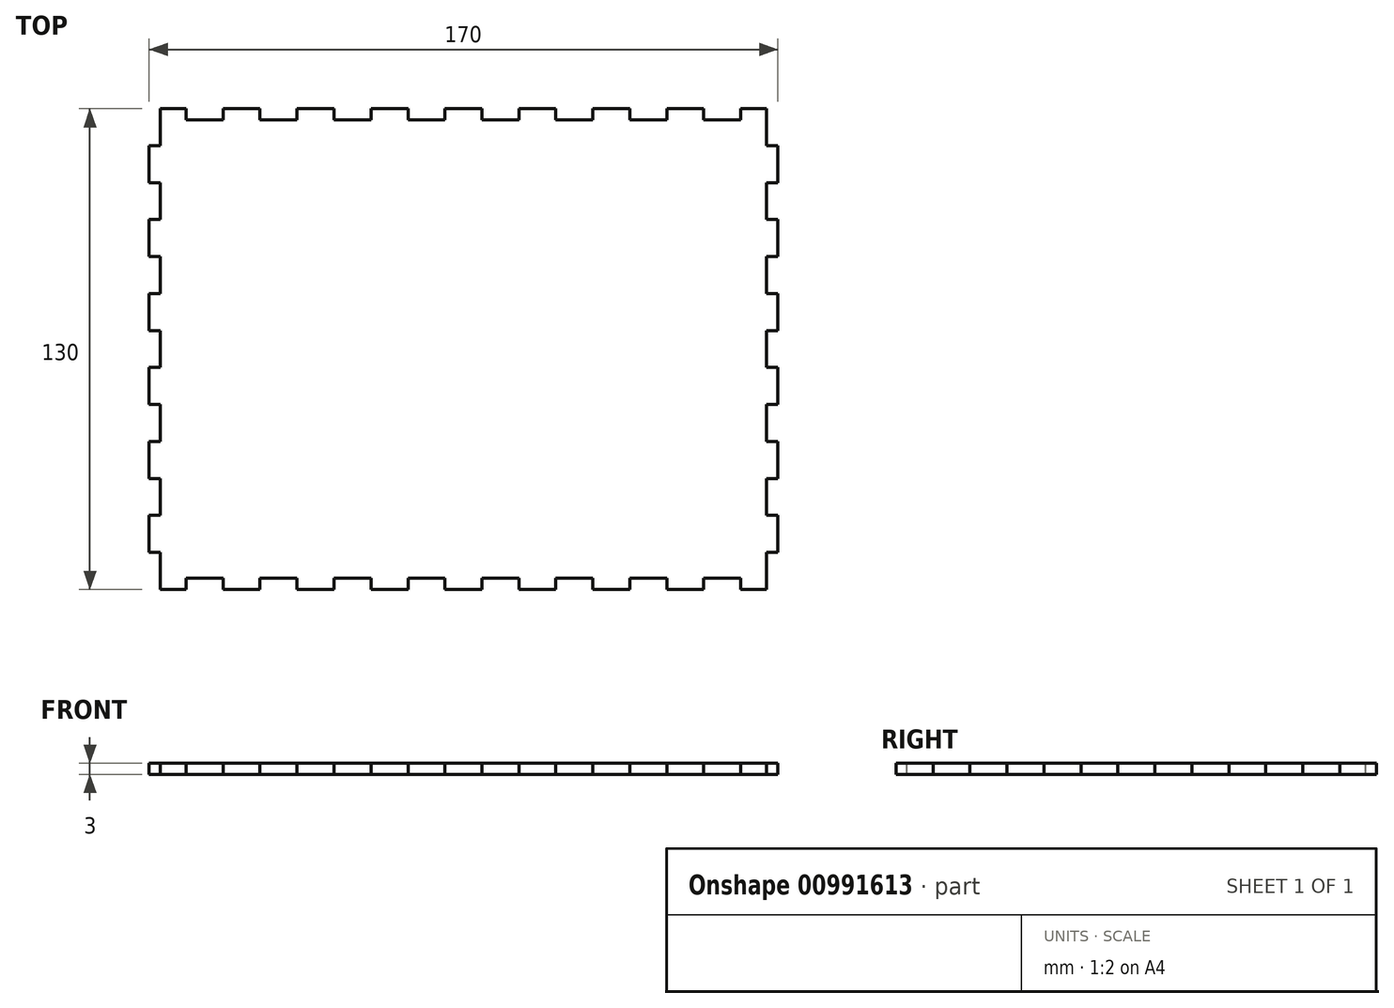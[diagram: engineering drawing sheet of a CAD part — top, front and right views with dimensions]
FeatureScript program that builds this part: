
annotation { "Feature Type Name" : "Feature", "Feature Type Description" : "" }
export const myFeature = defineFeature(function(context is Context, id is Id, definition is map)
    precondition{}
    {
        {
            var Q0;
            Q0=qCreatedBy(makeId("Top.planeOp"),FACE);
            var sketch = newSketch(context, id + "F0", { "sketchPlane" : qUnion([Q0])});
            skLineSegment(sketch, "E0.bottom", {"start": v(85, -65) * mm, "end": v(-85, -65) * mm});
            skLineSegment(sketch, "E0.top", {"start": v(85, 65) * mm, "end": v(-85, 65) * mm});
            skLineSegment(sketch, "E0.left", {"start": v(85, -65) * mm, "end": v(85, 65) * mm});
            skLineSegment(sketch, "E0.right", {"start": v(-85, -65) * mm, "end": v(-85, 65) * mm});
            skPoint(sketch, "E0.middle", {"position": v(0, 0) * mm});
            skSolve(sketch);
        }
        {
            var Q0;
            Q0=qSketchRegion(id+"F0",true);
            extrude(context, id + "F1", {"entities" : qUnion([Q0]), "depth" : 3 * mm, "offsetDistance" : 25 * mm});
        }
        {
            var Q0;
            Q0=makeQuery(id+"F1.opExtrude","CAP_FACE",FACE,{"disambiguationData":[OSD([sQuery(id+"F0.wireOp",EDGE,"E0.bottom"),sQuery(id+"F0.wireOp",EDGE,"E0.top"),sQuery(id+"F0.wireOp",EDGE,"E0.left"),sQuery(id+"F0.wireOp",EDGE,"E0.right")])],"isStart":false});
            var sketch = newSketch(context, id + "F2", { "sketchPlane" : qUnion([Q0])});
            skLineSegment(sketch, "E1.bottom", {"start": v(-75, -65) * mm, "end": v(-65, -65) * mm});
            skLineSegment(sketch, "E1.top", {"start": v(-75, -62) * mm, "end": v(-65, -62) * mm});
            skLineSegment(sketch, "E1.left", {"start": v(-75, -65) * mm, "end": v(-75, -62) * mm});
            skLineSegment(sketch, "E1.right", {"start": v(-65, -65) * mm, "end": v(-65, -62) * mm});
            skLineSegment(sketch, "E2.1.0.0", {"start": v(-55, -65) * mm, "end": v(-45, -65) * mm});
            skLineSegment(sketch, "E2.1.0.1", {"start": v(-55, -62) * mm, "end": v(-45, -62) * mm});
            skLineSegment(sketch, "E2.1.0.2", {"start": v(-55, -65) * mm, "end": v(-55, -62) * mm});
            skLineSegment(sketch, "E2.1.0.3", {"start": v(-45, -65) * mm, "end": v(-45, -62) * mm});
            skLineSegment(sketch, "E2.2.0.0", {"start": v(-35, -65) * mm, "end": v(-25, -65) * mm});
            skLineSegment(sketch, "E2.2.0.1", {"start": v(-35, -62) * mm, "end": v(-25, -62) * mm});
            skLineSegment(sketch, "E2.2.0.2", {"start": v(-35, -65) * mm, "end": v(-35, -62) * mm});
            skLineSegment(sketch, "E2.2.0.3", {"start": v(-25, -65) * mm, "end": v(-25, -62) * mm});
            skLineSegment(sketch, "E2.3.0.0", {"start": v(-15, -65) * mm, "end": v(-5, -65) * mm});
            skLineSegment(sketch, "E2.3.0.1", {"start": v(-15, -62) * mm, "end": v(-5, -62) * mm});
            skLineSegment(sketch, "E2.3.0.2", {"start": v(-15, -65) * mm, "end": v(-15, -62) * mm});
            skLineSegment(sketch, "E2.3.0.3", {"start": v(-5, -65) * mm, "end": v(-5, -62) * mm});
            skLineSegment(sketch, "E2.4.0.0", {"start": v(5, -65) * mm, "end": v(15, -65) * mm});
            skLineSegment(sketch, "E2.4.0.1", {"start": v(5, -62) * mm, "end": v(15, -62) * mm});
            skLineSegment(sketch, "E2.4.0.2", {"start": v(5, -65) * mm, "end": v(5, -62) * mm});
            skLineSegment(sketch, "E2.4.0.3", {"start": v(15, -65) * mm, "end": v(15, -62) * mm});
            skLineSegment(sketch, "E2.5.0.0", {"start": v(25, -65) * mm, "end": v(35, -65) * mm});
            skLineSegment(sketch, "E2.5.0.1", {"start": v(25, -62) * mm, "end": v(35, -62) * mm});
            skLineSegment(sketch, "E2.5.0.2", {"start": v(25, -65) * mm, "end": v(25, -62) * mm});
            skLineSegment(sketch, "E2.5.0.3", {"start": v(35, -65) * mm, "end": v(35, -62) * mm});
            skLineSegment(sketch, "E2.6.0.0", {"start": v(45, -65) * mm, "end": v(55, -65) * mm});
            skLineSegment(sketch, "E2.6.0.1", {"start": v(45, -62) * mm, "end": v(55, -62) * mm});
            skLineSegment(sketch, "E2.6.0.2", {"start": v(45, -65) * mm, "end": v(45, -62) * mm});
            skLineSegment(sketch, "E2.6.0.3", {"start": v(55, -65) * mm, "end": v(55, -62) * mm});
            skLineSegment(sketch, "E2.7.0.0", {"start": v(65, -65) * mm, "end": v(75, -65) * mm});
            skLineSegment(sketch, "E2.7.0.1", {"start": v(65, -62) * mm, "end": v(75, -62) * mm});
            skLineSegment(sketch, "E2.7.0.2", {"start": v(65, -65) * mm, "end": v(65, -62) * mm});
            skLineSegment(sketch, "E2.7.0.3", {"start": v(75, -65) * mm, "end": v(75, -62) * mm});
            skLineSegment(sketch, "E2.direction1", {"start": v(-75, -65) * mm, "end": v(-55, -65) * mm, "construction": true});
            skLineSegment(sketch, "E3.bottom", {"start": v(-85, -65) * mm, "end": v(-82, -65) * mm});
            skLineSegment(sketch, "E3.top", {"start": v(-85, -55) * mm, "end": v(-82, -55) * mm});
            skLineSegment(sketch, "E3.left", {"start": v(-85, -65) * mm, "end": v(-85, -55) * mm});
            skLineSegment(sketch, "E3.right", {"start": v(-82, -65) * mm, "end": v(-82, -55) * mm});
            skLineSegment(sketch, "E4.0.1.0", {"start": v(-85, -45) * mm, "end": v(-82, -45) * mm});
            skLineSegment(sketch, "E4.0.1.1", {"start": v(-85, -35) * mm, "end": v(-82, -35) * mm});
            skLineSegment(sketch, "E4.0.1.2", {"start": v(-85, -45) * mm, "end": v(-85, -35) * mm});
            skLineSegment(sketch, "E4.0.1.3", {"start": v(-82, -45) * mm, "end": v(-82, -35) * mm});
            skLineSegment(sketch, "E4.0.2.0", {"start": v(-85, -25) * mm, "end": v(-82, -25) * mm});
            skLineSegment(sketch, "E4.0.2.1", {"start": v(-85, -15) * mm, "end": v(-82, -15) * mm});
            skLineSegment(sketch, "E4.0.2.2", {"start": v(-85, -25) * mm, "end": v(-85, -15) * mm});
            skLineSegment(sketch, "E4.0.2.3", {"start": v(-82, -25) * mm, "end": v(-82, -15) * mm});
            skLineSegment(sketch, "E4.0.3.0", {"start": v(-85, -5) * mm, "end": v(-82, -5) * mm});
            skLineSegment(sketch, "E4.0.3.1", {"start": v(-85, 5) * mm, "end": v(-82, 5) * mm});
            skLineSegment(sketch, "E4.0.3.2", {"start": v(-85, -5) * mm, "end": v(-85, 5) * mm});
            skLineSegment(sketch, "E4.0.3.3", {"start": v(-82, -5) * mm, "end": v(-82, 5) * mm});
            skLineSegment(sketch, "E4.0.4.0", {"start": v(-85, 15) * mm, "end": v(-82, 15) * mm});
            skLineSegment(sketch, "E4.0.4.1", {"start": v(-85, 25) * mm, "end": v(-82, 25) * mm});
            skLineSegment(sketch, "E4.0.4.2", {"start": v(-85, 15) * mm, "end": v(-85, 25) * mm});
            skLineSegment(sketch, "E4.0.4.3", {"start": v(-82, 15) * mm, "end": v(-82, 25) * mm});
            skLineSegment(sketch, "E4.0.5.0", {"start": v(-85, 35) * mm, "end": v(-82, 35) * mm});
            skLineSegment(sketch, "E4.0.5.1", {"start": v(-85, 45) * mm, "end": v(-82, 45) * mm});
            skLineSegment(sketch, "E4.0.5.2", {"start": v(-85, 35) * mm, "end": v(-85, 45) * mm});
            skLineSegment(sketch, "E4.0.5.3", {"start": v(-82, 35) * mm, "end": v(-82, 45) * mm});
            skLineSegment(sketch, "E4.0.6.0", {"start": v(-85, 55) * mm, "end": v(-82, 55) * mm});
            skLineSegment(sketch, "E4.0.6.1", {"start": v(-85, 65) * mm, "end": v(-82, 65) * mm});
            skLineSegment(sketch, "E4.0.6.2", {"start": v(-85, 55) * mm, "end": v(-85, 65) * mm});
            skLineSegment(sketch, "E4.0.6.3", {"start": v(-82, 55) * mm, "end": v(-82, 65) * mm});
            skLineSegment(sketch, "E4.direction1", {"start": v(-85, -65) * mm, "end": v(-60, -65) * mm, "construction": true});
            skLineSegment(sketch, "E4.direction2", {"start": v(-85, -65) * mm, "end": v(-85, -45) * mm, "construction": true});
            skLineSegment(sketch, "E5", {"start": v(85, 0) * mm, "end": v(-85, 0) * mm, "construction": true});
            skLineSegment(sketch, "E6", {"start": v(0, 65) * mm, "end": v(0, -65) * mm, "construction": true});
            skLineSegment(sketch, "E7.MirrorCS", {"start": v(85, -65) * mm, "end": v(85, -55) * mm});
            skLineSegment(sketch, "E8.MirrorCS", {"start": v(82, -45) * mm, "end": v(82, -35) * mm});
            skLineSegment(sketch, "E9.MirrorCS", {"start": v(85, -45) * mm, "end": v(85, -35) * mm});
            skLineSegment(sketch, "E10.MirrorCS", {"start": v(82, 15) * mm, "end": v(82, 25) * mm});
            skLineSegment(sketch, "E11.MirrorCS", {"start": v(85, 15) * mm, "end": v(85, 25) * mm});
            skLineSegment(sketch, "E12.MirrorCS", {"start": v(85, 55) * mm, "end": v(82, 55) * mm});
            skLineSegment(sketch, "E13.MirrorCS", {"start": v(85, -5) * mm, "end": v(85, 5) * mm});
            skLineSegment(sketch, "E14.MirrorCS", {"start": v(85, 55) * mm, "end": v(85, 65) * mm});
            skLineSegment(sketch, "E15.MirrorCS", {"start": v(85, -5) * mm, "end": v(82, -5) * mm});
            skLineSegment(sketch, "E16.MirrorCS", {"start": v(85, 65) * mm, "end": v(82, 65) * mm});
            skLineSegment(sketch, "E17.MirrorCS", {"start": v(82, 55) * mm, "end": v(82, 65) * mm});
            skLineSegment(sketch, "E18.MirrorCS", {"start": v(85, 15) * mm, "end": v(82, 15) * mm});
            skLineSegment(sketch, "E19.MirrorCS", {"start": v(85, -25) * mm, "end": v(85, -15) * mm});
            skLineSegment(sketch, "E20.MirrorCS", {"start": v(82, -5) * mm, "end": v(82, 5) * mm});
            skLineSegment(sketch, "E21.MirrorCS", {"start": v(85, -35) * mm, "end": v(82, -35) * mm});
            skLineSegment(sketch, "E22.MirrorCS", {"start": v(85, -55) * mm, "end": v(82, -55) * mm});
            skLineSegment(sketch, "E23.MirrorCS", {"start": v(85, -45) * mm, "end": v(82, -45) * mm});
            skLineSegment(sketch, "E24.MirrorCS", {"start": v(85, 25) * mm, "end": v(82, 25) * mm});
            skLineSegment(sketch, "E25.MirrorCS", {"start": v(85, 35) * mm, "end": v(82, 35) * mm});
            skLineSegment(sketch, "E26.MirrorCS", {"start": v(85, 5) * mm, "end": v(82, 5) * mm});
            skLineSegment(sketch, "E27.MirrorCS", {"start": v(82, -65) * mm, "end": v(82, -55) * mm});
            skLineSegment(sketch, "E28.MirrorCS", {"start": v(85, -15) * mm, "end": v(82, -15) * mm});
            skLineSegment(sketch, "E29.MirrorCS", {"start": v(85, -65) * mm, "end": v(85, -45) * mm, "construction": true});
            skLineSegment(sketch, "E30.MirrorCS", {"start": v(85, 45) * mm, "end": v(82, 45) * mm});
            skLineSegment(sketch, "E31.MirrorCS", {"start": v(82, 35) * mm, "end": v(82, 45) * mm});
            skLineSegment(sketch, "E32.MirrorCS", {"start": v(85, 35) * mm, "end": v(85, 45) * mm});
            skLineSegment(sketch, "E33.MirrorCS", {"start": v(85, -25) * mm, "end": v(82, -25) * mm});
            skLineSegment(sketch, "E34.MirrorCS", {"start": v(82, -25) * mm, "end": v(82, -15) * mm});
            skLineSegment(sketch, "E35.MirrorCS", {"start": v(85, -65) * mm, "end": v(82, -65) * mm});
            skLineSegment(sketch, "E36.MirrorCS", {"start": v(15, 65) * mm, "end": v(15, 62) * mm});
            skLineSegment(sketch, "E37.MirrorCS", {"start": v(-65, 65) * mm, "end": v(-65, 62) * mm});
            skLineSegment(sketch, "E38.MirrorCS", {"start": v(45, 65) * mm, "end": v(45, 62) * mm});
            skLineSegment(sketch, "E39.MirrorCS", {"start": v(5, 65) * mm, "end": v(5, 62) * mm});
            skLineSegment(sketch, "E40.MirrorCS", {"start": v(75, 65) * mm, "end": v(75, 62) * mm});
            skLineSegment(sketch, "E41.MirrorCS", {"start": v(-35, 65) * mm, "end": v(-35, 62) * mm});
            skLineSegment(sketch, "E42.MirrorCS", {"start": v(65, 65) * mm, "end": v(65, 62) * mm});
            skLineSegment(sketch, "E43.MirrorCS", {"start": v(-45, 65) * mm, "end": v(-45, 62) * mm});
            skLineSegment(sketch, "E44.MirrorCS", {"start": v(35, 65) * mm, "end": v(35, 62) * mm});
            skLineSegment(sketch, "E45.MirrorCS", {"start": v(-75, 65) * mm, "end": v(-75, 62) * mm});
            skLineSegment(sketch, "E46.MirrorCS", {"start": v(-15, 65) * mm, "end": v(-15, 62) * mm});
            skLineSegment(sketch, "E47.MirrorCS", {"start": v(55, 65) * mm, "end": v(55, 62) * mm});
            skLineSegment(sketch, "E48.MirrorCS", {"start": v(-5, 65) * mm, "end": v(-5, 62) * mm});
            skLineSegment(sketch, "E49.MirrorCS", {"start": v(25, 65) * mm, "end": v(25, 62) * mm});
            skLineSegment(sketch, "E50.MirrorCS", {"start": v(-25, 65) * mm, "end": v(-25, 62) * mm});
            skLineSegment(sketch, "E51.MirrorCS", {"start": v(-55, 65) * mm, "end": v(-55, 62) * mm});
            skLineSegment(sketch, "E52.MirrorCS", {"start": v(-75, 65) * mm, "end": v(-65, 65) * mm});
            skLineSegment(sketch, "E53.MirrorCS", {"start": v(25, 65) * mm, "end": v(35, 65) * mm});
            skLineSegment(sketch, "E54.MirrorCS", {"start": v(5, 65) * mm, "end": v(15, 65) * mm});
            skLineSegment(sketch, "E55.MirrorCS", {"start": v(-55, 62) * mm, "end": v(-45, 62) * mm});
            skLineSegment(sketch, "E56.MirrorCS", {"start": v(5, 62) * mm, "end": v(15, 62) * mm});
            skLineSegment(sketch, "E57.MirrorCS", {"start": v(-55, 65) * mm, "end": v(-45, 65) * mm});
            skLineSegment(sketch, "E58.MirrorCS", {"start": v(65, 62) * mm, "end": v(75, 62) * mm});
            skLineSegment(sketch, "E59.MirrorCS", {"start": v(-15, 62) * mm, "end": v(-5, 62) * mm});
            skLineSegment(sketch, "E60.MirrorCS", {"start": v(-35, 62) * mm, "end": v(-25, 62) * mm});
            skLineSegment(sketch, "E61.MirrorCS", {"start": v(-75, 65) * mm, "end": v(-55, 65) * mm, "construction": true});
            skLineSegment(sketch, "E62.MirrorCS", {"start": v(-35, 65) * mm, "end": v(-25, 65) * mm});
            skLineSegment(sketch, "E63.MirrorCS", {"start": v(45, 62) * mm, "end": v(55, 62) * mm});
            skLineSegment(sketch, "E64.MirrorCS", {"start": v(-15, 65) * mm, "end": v(-5, 65) * mm});
            skLineSegment(sketch, "E65.MirrorCS", {"start": v(-75, 62) * mm, "end": v(-65, 62) * mm});
            skLineSegment(sketch, "E66.MirrorCS", {"start": v(45, 65) * mm, "end": v(55, 65) * mm});
            skLineSegment(sketch, "E67.MirrorCS", {"start": v(25, 62) * mm, "end": v(35, 62) * mm});
            skLineSegment(sketch, "E68.MirrorCS", {"start": v(65, 65) * mm, "end": v(75, 65) * mm});
            skSolve(sketch);
        }
        {
            var Q0;
            Q0=qSketchRegion(id+"F2",true);
            extrude(context, id + "F3", {"entities" : qUnion([Q0]), "operationType" : NewBodyOperationType.REMOVE, "endBound" : BoundingType.THROUGH_ALL, "oppositeDirection" : true, "depth" : 25 * mm, "offsetDistance" : 25 * mm});
        }
    });
